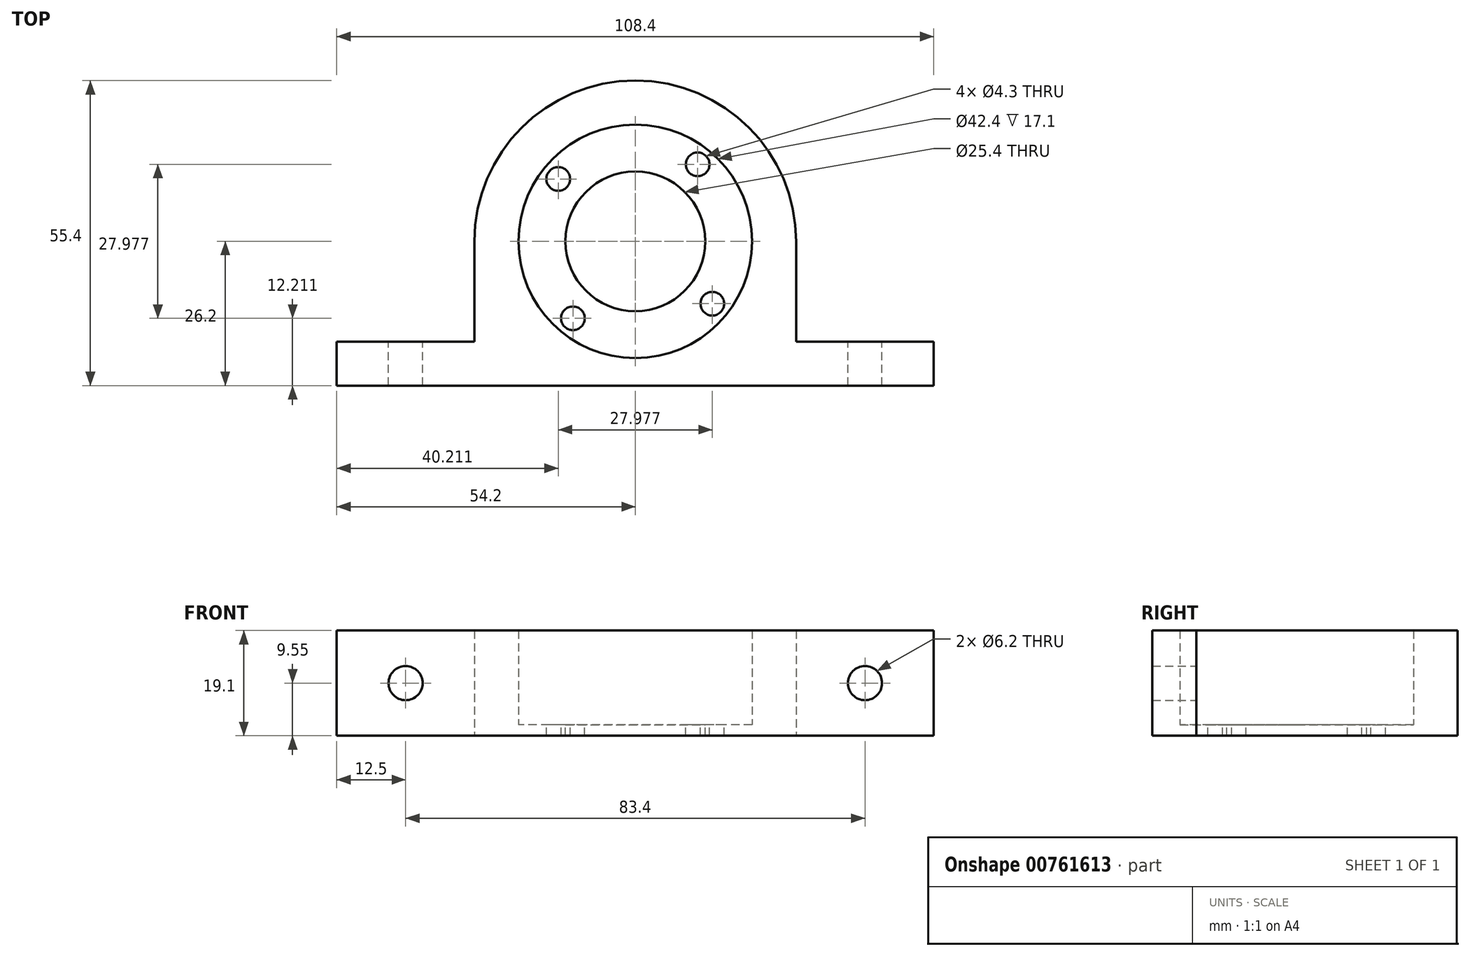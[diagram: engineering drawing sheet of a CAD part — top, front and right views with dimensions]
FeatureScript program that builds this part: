
annotation { "Feature Type Name" : "Feature", "Feature Type Description" : "" }
export const myFeature = defineFeature(function(context is Context, id is Id, definition is map)
    precondition{}
    {
        {
            var Q0;
            Q0=qCreatedBy(makeId("Top.planeOp"),FACE);
            var sketch = newSketch(context, id + "F0", { "sketchPlane" : qUnion([Q0])});
            skCircle(sketch, "E0", {"center": v(0, 0) * mm, "radius": 21.2 * mm});
            skCircle(sketch, "E1", {"center": v(0, 0) * mm, "radius": 26.2 * mm, "construction": true});
            skLineSegment(sketch, "E2", {"start": v(-64.12, -26.2) * mm, "end": v(71.3, -26.2) * mm, "construction": true});
            skLineSegment(sketch, "E3", {"start": v(54.2, -26.2) * mm, "end": v(-54.2, -26.2) * mm});
            skLineSegment(sketch, "E4", {"start": v(-54.2, -26.2) * mm, "end": v(-54.2, -18.2) * mm});
            skLineSegment(sketch, "E5", {"start": v(-54.2, -18.2) * mm, "end": v(-29.2, -18.2) * mm});
            skLineSegment(sketch, "E6", {"start": v(-29.2, -18.2) * mm, "end": v(-29.2, 0) * mm});
            skLineSegment(sketch, "E7", {"start": v(29.2, 0) * mm, "end": v(29.2, -18.2) * mm});
            skLineSegment(sketch, "E8", {"start": v(29.2, -18.2) * mm, "end": v(54.2, -18.2) * mm});
            skLineSegment(sketch, "E9", {"start": v(54.2, -18.2) * mm, "end": v(54.2, -26.2) * mm});
            skArc(sketch, "E10", {"start": v(29.2, 0) * mm, "mid": v(0, 29.2) * mm, "end": v(-29.2, 0) * mm});
            skSolve(sketch);
        }
        {
            var Q0;
            Q0=makeQuery(id+"F0.imprint","IMPRINT",FACE,{"disambiguationData":[TD([[makeQuery(id+"F0.imprint","IMPRINT",EDGE,{"derivedFrom":sQuery(id+"F0.wireOp",EDGE,"E0")}),-1.0]])]});
            extrude(context, id + "F1", {"entities" : qUnion([Q0]), "depth" : 17.1 * mm, "offsetDistance" : 25 * mm});
        }
        {
            var Q0;
            Q0=makeQuery(id+"F1.opExtrude","CAP_FACE",FACE,{"disambiguationData":[OSD([sQuery(id+"F0.wireOp",EDGE,"E0"),sQuery(id+"F0.wireOp",EDGE,"E3"),sQuery(id+"F0.wireOp",EDGE,"E4"),sQuery(id+"F0.wireOp",EDGE,"E5"),sQuery(id+"F0.wireOp",EDGE,"E6"),sQuery(id+"F0.wireOp",EDGE,"E7"),sQuery(id+"F0.wireOp",EDGE,"E8"),sQuery(id+"F0.wireOp",EDGE,"E9"),sQuery(id+"F0.wireOp",EDGE,"E10")])],"isStart":true});
            var sketch = newSketch(context, id + "F2", { "sketchPlane" : qUnion([Q0])});
            skCircle(sketch, "E11", {"center": v(0, 0) * mm, "radius": 12.7 * mm});
            skArc(sketch, "E12", {"start": v(-29.2, 0) * mm, "mid": v(0, -29.2) * mm, "end": v(29.2, 0) * mm});
            skLineSegment(sketch, "E13", {"start": v(-29.2, 0) * mm, "end": v(-29.2, 18.2) * mm});
            skLineSegment(sketch, "E14", {"start": v(29.2, 0) * mm, "end": v(29.2, 18.2) * mm});
            skLineSegment(sketch, "E15", {"start": v(54.2, 26.2) * mm, "end": v(-54.2, 26.2) * mm});
            skLineSegment(sketch, "E16", {"start": v(-54.2, 26.2) * mm, "end": v(-54.2, 18.2) * mm});
            skLineSegment(sketch, "E17", {"start": v(-54.2, 18.2) * mm, "end": v(-29.2, 18.2) * mm});
            skLineSegment(sketch, "E18", {"start": v(54.2, 26.2) * mm, "end": v(54.2, 18.2) * mm});
            skLineSegment(sketch, "E19", {"start": v(54.2, 18.2) * mm, "end": v(29.2, 18.2) * mm});
            skSolve(sketch);
        }
        {
            var Q0;
            Q0 = qSketchRegion(id + "F2", true);
            extrude(context, id + "F3", {"entities" : qUnion([Q0]), "operationType" : NewBodyOperationType.ADD, "depth" : 2 * mm, "offsetDistance" : 25 * mm});
        }
        {
            var Q0;
            Q0=makeQuery(id+"F3.opExtrude","CAP_FACE",FACE,{"disambiguationData":[OSD([sQuery(id+"F2.wireOp",EDGE,"E11"),sQuery(id+"F2.wireOp",EDGE,"E12"),sQuery(id+"F2.wireOp",EDGE,"E13"),sQuery(id+"F2.wireOp",EDGE,"E14"),sQuery(id+"F2.wireOp",EDGE,"E15")])],"isStart":true});
            var sketch = newSketch(context, id + "F4", { "sketchPlane" : qUnion([Q0])});
            skCircle(sketch, "E20", {"center": v(0, 0) * mm, "radius": 12.7 * mm});
            skCircle(sketch, "E21", {"center": v(0, 0) * mm, "radius": 21.2 * mm});
            skSolve(sketch);
        }
        {
            var Q0;
            Q0=makeQuery(id+"F4.imprint","IMPRINT",FACE,{"disambiguationData":[TD([[makeQuery(id+"F4.imprint","IMPRINT",EDGE,{"derivedFrom":sQuery(id+"F4.wireOp",EDGE,"E20")}),1.0]])]});
            var sketch = newSketch(context, id + "F5", { "sketchPlane" : qUnion([Q0])});
            skCircle(sketch, "E22", {"center": v(0, 0) * mm, "radius": 18 * mm, "construction": true});
            skLineSegment(sketch, "E23.bottom", {"start": v(-13.99, 11.33) * mm, "end": v(-11.33, -13.99) * mm, "construction": true});
            skLineSegment(sketch, "E23.top", {"start": v(11.33, 13.99) * mm, "end": v(13.99, -11.33) * mm, "construction": true});
            skLineSegment(sketch, "E23.left", {"start": v(-13.99, 11.33) * mm, "end": v(11.33, 13.99) * mm, "construction": true});
            skLineSegment(sketch, "E23.right", {"start": v(-11.33, -13.99) * mm, "end": v(13.99, -11.33) * mm, "construction": true});
            skCircle(sketch, "E24", {"center": v(11.33, 13.99) * mm, "radius": 2.15 * mm});
            skCircle(sketch, "E25.1.0", {"center": v(-13.99, 11.33) * mm, "radius": 2.15 * mm});
            skCircle(sketch, "E25.2.0", {"center": v(-11.33, -13.99) * mm, "radius": 2.15 * mm});
            skCircle(sketch, "E25.3.0", {"center": v(13.99, -11.33) * mm, "radius": 2.15 * mm});
            skLineSegment(sketch, "E26", {"start": v(12.66, 1.33) * mm, "end": v(0, 0) * mm, "construction": true});
            skSolve(sketch);
        }
        {
            var Q0;
            Q0=makeQuery(id+"F5.imprint","IMPRINT",FACE,{"disambiguationData":[TD([[makeQuery(id+"F5.imprint","IMPRINT",EDGE,{"derivedFrom":sQuery(id+"F5.wireOp",EDGE,"E24")}),1.0]])]});
            var Q1;
            Q1=makeQuery(id+"F5.imprint","IMPRINT",FACE,{"disambiguationData":[TD([[makeQuery(id+"F5.imprint","IMPRINT",EDGE,{"derivedFrom":sQuery(id+"F5.wireOp",EDGE,"E25.3.0")}),1.0]])]});
            var Q2;
            Q2=makeQuery(id+"F5.imprint","IMPRINT",FACE,{"disambiguationData":[TD([[makeQuery(id+"F5.imprint","IMPRINT",EDGE,{"derivedFrom":sQuery(id+"F5.wireOp",EDGE,"E25.2.0")}),1.0]])]});
            var Q3;
            Q3=makeQuery(id+"F5.imprint","IMPRINT",FACE,{"disambiguationData":[TD([[makeQuery(id+"F5.imprint","IMPRINT",EDGE,{"derivedFrom":sQuery(id+"F5.wireOp",EDGE,"E25.1.0")}),1.0]])]});
            extrude(context, id + "F6", {"entities" : qUnion([Q0, Q1, Q2, Q3]), "operationType" : NewBodyOperationType.REMOVE, "oppositeDirection" : true, "depth" : 25 * mm, "offsetDistance" : 25 * mm});
        }
        {
            var Q0;
            Q0=makeQuery(id+"F1.opExtrude","SWEPT_FACE",FACE,{"disambiguationData":[OSD([sQuery(id+"F0.wireOp",EDGE,"E5")])]});
            var sketch = newSketch(context, id + "F7", { "sketchPlane" : qUnion([Q0])});
            skLineSegment(sketch, "E27", {"start": v(41.7, -2) * mm, "end": v(41.7, 17.1) * mm, "construction": true});
            skLineSegment(sketch, "E28", {"start": v(-41.7, -2) * mm, "end": v(-41.7, 17.1) * mm, "construction": true});
            skCircle(sketch, "E29", {"center": v(41.7, 7.55) * mm, "radius": 3.1 * mm});
            skCircle(sketch, "E30", {"center": v(-41.7, 7.55) * mm, "radius": 3.1 * mm});
            skSolve(sketch);
        }
        {
            var Q0;
            Q0 = qSketchRegion(id + "F7", true);
            extrude(context, id + "F8", {"entities" : qUnion([Q0]), "operationType" : NewBodyOperationType.REMOVE, "endBound" : BoundingType.THROUGH_ALL, "oppositeDirection" : true, "depth" : 25 * mm, "offsetDistance" : 25 * mm});
        }
    });
